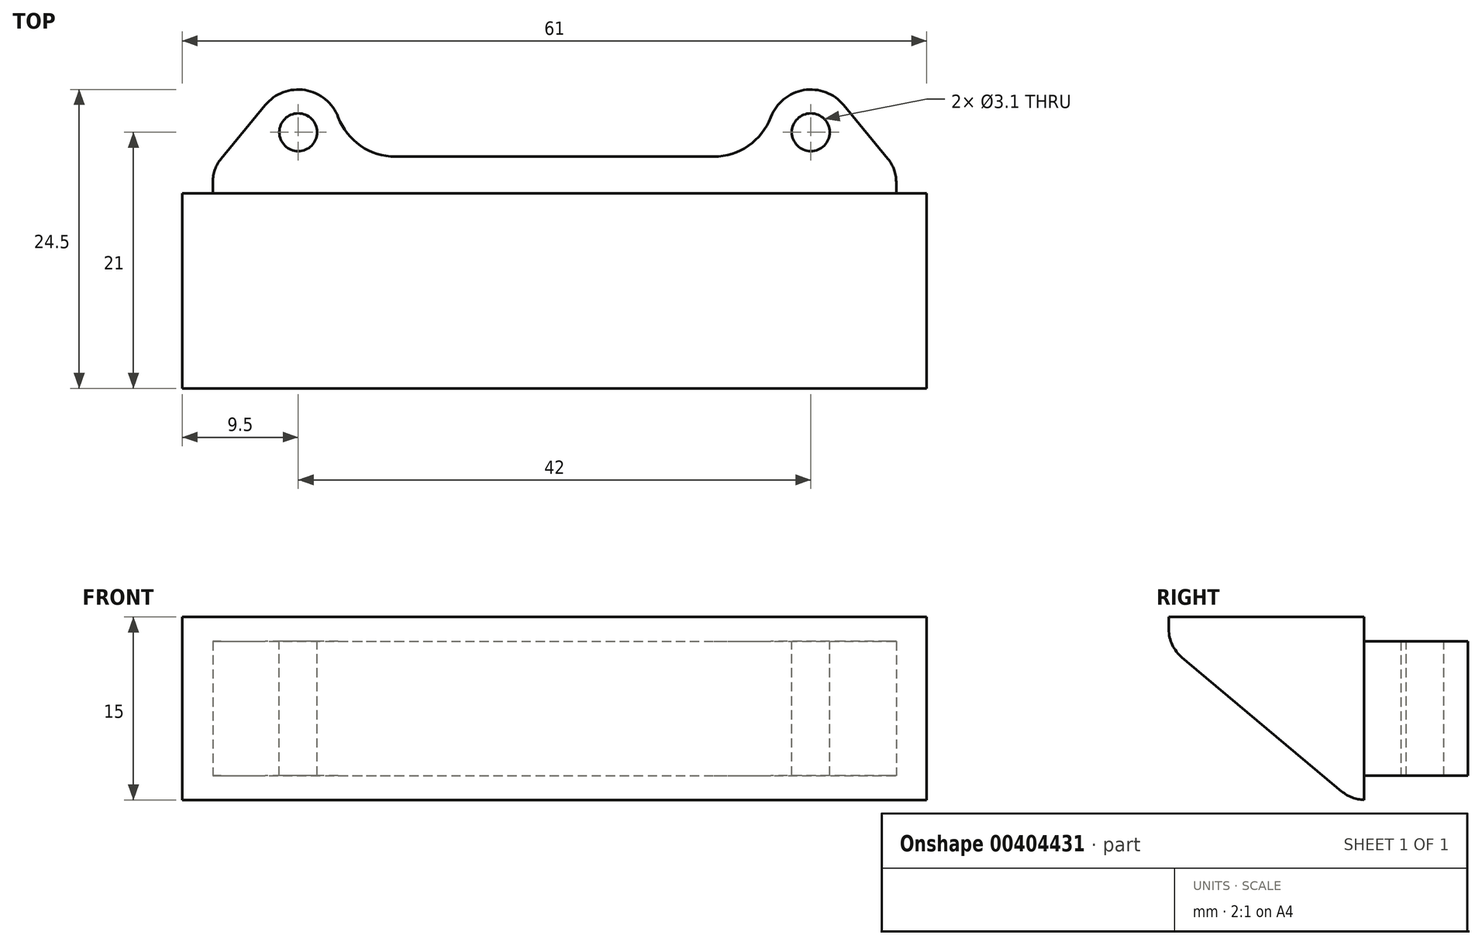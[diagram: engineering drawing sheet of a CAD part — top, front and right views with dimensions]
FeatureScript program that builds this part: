
annotation { "Feature Type Name" : "Feature", "Feature Type Description" : "" }
export const myFeature = defineFeature(function(context is Context, id is Id, definition is map)
    precondition{}
    {
        {
            var Q0;
            Q0=qCreatedBy(makeId("Top.planeOp"),FACE);
            var sketch = newSketch(context, id + "F0", { "sketchPlane" : qUnion([Q0])});
            skCircle(sketch, "E0", {"center": v(-21, 5) * mm, "radius": 3.5 * mm});
            skCircle(sketch, "E1", {"center": v(21, 5) * mm, "radius": 3.5 * mm});
            skLineSegment(sketch, "E2", {"start": v(-21, 5) * mm, "end": v(21, 5) * mm, "construction": true});
            skLineSegment(sketch, "E3", {"start": v(0, 5) * mm, "end": v(0, 0) * mm});
            skLineSegment(sketch, "E4", {"start": v(30.5, -16) * mm, "end": v(-30.5, -16) * mm});
            skLineSegment(sketch, "E5", {"start": v(-30.5, -16) * mm, "end": v(-30.5, 0) * mm});
            skLineSegment(sketch, "E6", {"start": v(-30.5, 0) * mm, "end": v(-28, 0) * mm});
            skLineSegment(sketch, "E7", {"start": v(30.5, -16) * mm, "end": v(30.5, 0) * mm});
            skLineSegment(sketch, "E8", {"start": v(30.5, 0) * mm, "end": v(28, 0) * mm});
            skLineSegment(sketch, "E9", {"start": v(-17.5, 5) * mm, "end": v(-17.5, 3) * mm});
            skLineSegment(sketch, "E10", {"start": v(-17.5, 3) * mm, "end": v(17.5, 3) * mm});
            skLineSegment(sketch, "E11", {"start": v(17.5, 3) * mm, "end": v(17.5, 5) * mm});
            skLineSegment(sketch, "E12", {"start": v(-28, 0) * mm, "end": v(-28, 2) * mm});
            skLineSegment(sketch, "E13", {"start": v(-28, 2) * mm, "end": v(-23.7, 7.22) * mm});
            skLineSegment(sketch, "E14", {"start": v(28, 0) * mm, "end": v(28, 2) * mm});
            skLineSegment(sketch, "E15", {"start": v(28, 2) * mm, "end": v(23.7, 7.22) * mm});
            skLineSegment(sketch, "E16", {"start": v(0, -16) * mm, "end": v(0, 0) * mm});
            skLineSegment(sketch, "E17", {"start": v(-28, 0) * mm, "end": v(28, 0) * mm});
            skSolve(sketch);
        }
        {
            var Q0;
            {var subQ1=sQuery(id+"F0.wireOp",EDGE,"E7");Q0=makeQuery(id+"F0.imprint","IMPRINT",FACE,{"disambiguationData":[TD([[makeQuery(id+"F0.imprint","IMPRINT",EDGE,{"derivedFrom":subQ1}),1.0]])]});}
            var Q1;
            {var subQ2=sQuery(id+"F0.wireOp",EDGE,"E5");Q1=makeQuery(id+"F0.imprint","IMPRINT",FACE,{"disambiguationData":[TD([[makeQuery(id+"F0.imprint","IMPRINT",EDGE,{"derivedFrom":subQ2}),-1.0]])]});}
            extrude(context, id + "F1", {"entities" : qUnion([Q0, Q1]), "endBound" : BoundingType.SYMMETRIC, "depth" : 15 * mm});
        }
        {
            var Q0;
            {var subQ1=sQuery(id+"F0.wireOp",EDGE,"E9");Q0=makeQuery(id+"F0.imprint","IMPRINT",FACE,{"disambiguationData":[TD([[makeQuery(id+"F0.imprint","IMPRINT",EDGE,{"derivedFrom":subQ1}),-1.0]])]});}
            var Q1;
            {var subQ0=sQuery(id+"F0.wireOp",EDGE,"E0");var subQ1=makeQuery(id+"F0.imprint","INTERSECT",VERTEX,{"derivedFrom":[subQ0,sQuery(id+"F0.wireOp",EDGE,"E9")]});Q1=makeQuery(id+"F0.imprint","IMPRINT",FACE,{"disambiguationData":[TD([[makeQuery(id+"F0.imprint","IMPRINT",EDGE,{"disambiguationData":[TD([[subQ1,1.0]])],"derivedFrom":subQ0}),1.0]])]});}
            var Q2;
            {var subQ0=sQuery(id+"F0.wireOp",EDGE,"E1");var subQ1=makeQuery(id+"F0.imprint","INTERSECT",VERTEX,{"derivedFrom":[subQ0,sQuery(id+"F0.wireOp",EDGE,"E11")]});Q2=makeQuery(id+"F0.imprint","IMPRINT",FACE,{"disambiguationData":[TD([[makeQuery(id+"F0.imprint","IMPRINT",EDGE,{"disambiguationData":[TD([[subQ1,1.0]])],"derivedFrom":subQ0}),1.0]])]});}
            var Q3;
            {var subQ0=sQuery(id+"F0.wireOp",EDGE,"E11");Q3=makeQuery(id+"F0.imprint","IMPRINT",FACE,{"disambiguationData":[TD([[makeQuery(id+"F0.imprint","IMPRINT",EDGE,{"derivedFrom":subQ0}),-1.0]])]});}
            extrude(context, id + "F2", {"entities" : qUnion([Q0, Q1, Q2, Q3]), "operationType" : NewBodyOperationType.ADD, "endBound" : BoundingType.SYMMETRIC, "depth" : 11 * mm});
        }
        {
            var Q0;
            Q0=makeQuery(id+"F1.opExtrude","CAP_EDGE",EDGE,{"disambiguationData":[OSD([sQuery(id+"F0.wireOp",EDGE,"E4")])],"isStart":true});
            chamfer(context, id + "F3", {"entities" : qUnion([Q0]), "chamferType" : ChamferType.OFFSET_ANGLE, "width" : 15 * mm, "oppositeDirection" : false, "angle" : 40 * degree, "tangentPropagation" : true});
        }
        {
            var Q0;
            Q0=makeQuery(id+"F2.opExtrude","CAP_FACE",FACE,{"disambiguationData":[OSD([sQuery(id+"F0.wireOp",EDGE,"E0"),sQuery(id+"F0.wireOp",EDGE,"E1"),sQuery(id+"F0.wireOp",EDGE,"E9"),sQuery(id+"F0.wireOp",EDGE,"E10"),sQuery(id+"F0.wireOp",EDGE,"E11"),sQuery(id+"F0.wireOp",EDGE,"E12"),sQuery(id+"F0.wireOp",EDGE,"E13"),sQuery(id+"F0.wireOp",EDGE,"E14"),sQuery(id+"F0.wireOp",EDGE,"E15"),sQuery(id+"F0.wireOp",EDGE,"E17")])],"isStart":false});
            var sketch = newSketch(context, id + "F4", { "sketchPlane" : qUnion([Q0])});
            skPoint(sketch, "E18", {"position": v(-21, 5) * mm});
            skPoint(sketch, "E19", {"position": v(21, 5) * mm});
            skSolve(sketch);
        }
        {
            var Q0;
            Q0=sQuery(id+"F4.wireOp",VERTEX,"E18");
            var Q1;
            Q1=sQuery(id+"F4.wireOp",VERTEX,"E19");
            var Q2;
            Q2=makeQuery(id+"F1.opExtrude","SWEPT_BODY",BODY,{"disambiguationData":[OSD([sQuery(id+"F0.wireOp",EDGE,"E4"),sQuery(id+"F0.wireOp",EDGE,"E5"),sQuery(id+"F0.wireOp",EDGE,"E6"),sQuery(id+"F0.wireOp",EDGE,"E7"),sQuery(id+"F0.wireOp",EDGE,"E8"),sQuery(id+"F0.wireOp",EDGE,"E17")])]});
            hole(context, id + "F5", {"style" : HoleStyle.SIMPLE, "endStyle" : HoleEndStyle.THROUGH, "holeDiameter" : 3.1 * mm, "tappedDepth" : 12 * mm, "tapClearance" : 3, "locations" : qUnion([Q0, Q1]), "scope" : qUnion([Q2])});
        }
        {
            var Q0;
            {var subQ0=sQuery(id+"F0.wireOp",EDGE,"E4");Q0=makeQuery(id+"F3.opChamfer","BLEND_EDGE",EDGE,{"blendedFrom":[makeQuery(id+"F1.opExtrude","CAP_EDGE",EDGE,{"disambiguationData":[OSD([subQ0])],"isStart":true}),makeQuery(id+"F1.opExtrude","SWEPT_FACE",FACE,{"disambiguationData":[OSD([subQ0])]})],"blendedInto":[makeQuery(id+"F1.opExtrude","SWEPT_FACE",FACE,{"disambiguationData":[OSD([subQ0])]})]});}
            fillet(context, id + "F6", {"entities" : qUnion([Q0]), "radius" : 3 * mm, "tangentPropagation" : true, "allowEdgeOverflow" : false});
        }
        {
            var Q0;
            {var subQ0=sQuery(id+"F0.wireOp",EDGE,"E4");Q0=makeQuery(id+"F3.opChamfer","BLEND_EDGE",EDGE,{"blendedFrom":[makeQuery(id+"F1.opExtrude","CAP_EDGE",EDGE,{"disambiguationData":[OSD([subQ0])],"isStart":true}),makeQuery(id+"F1.opExtrude","CAP_FACE",FACE,{"disambiguationData":[OSD([subQ0,sQuery(id+"F0.wireOp",EDGE,"E5"),sQuery(id+"F0.wireOp",EDGE,"E6"),sQuery(id+"F0.wireOp",EDGE,"E7"),sQuery(id+"F0.wireOp",EDGE,"E8"),sQuery(id+"F0.wireOp",EDGE,"E17")])],"isStart":true})],"blendedInto":[makeQuery(id+"F1.opExtrude","CAP_FACE",FACE,{"disambiguationData":[OSD([subQ0,sQuery(id+"F0.wireOp",EDGE,"E5"),sQuery(id+"F0.wireOp",EDGE,"E6"),sQuery(id+"F0.wireOp",EDGE,"E7"),sQuery(id+"F0.wireOp",EDGE,"E8"),sQuery(id+"F0.wireOp",EDGE,"E17")])],"isStart":true})]});}
            var Q1;
            Q1=makeQuery(id+"F2.opExtrude","SWEPT_EDGE",EDGE,{"disambiguationData":[OSD([sQuery(id+"F0.wireOp",EDGE,"E12"),sQuery(id+"F0.wireOp",EDGE,"E13")])]});
            var Q2;
            Q2=makeQuery(id+"F2.opExtrude","SWEPT_EDGE",EDGE,{"disambiguationData":[OSD([sQuery(id+"F0.wireOp",EDGE,"E14"),sQuery(id+"F0.wireOp",EDGE,"E15")])]});
            fillet(context, id + "F7", {"entities" : qUnion([Q0, Q1, Q2]), "radius" : 3 * mm, "tangentPropagation" : true, "allowEdgeOverflow" : false});
        }
        {
            var Q0;
            Q0=makeQuery(id+"F2.opExtrude","SWEPT_EDGE",EDGE,{"disambiguationData":[OSD([sQuery(id+"F0.wireOp",EDGE,"E10"),sQuery(id+"F0.wireOp",EDGE,"E11")])]});
            var Q1;
            Q1=makeQuery(id+"F2.opExtrude","SWEPT_EDGE",EDGE,{"disambiguationData":[OSD([sQuery(id+"F0.wireOp",EDGE,"E9"),sQuery(id+"F0.wireOp",EDGE,"E10")])]});
            fillet(context, id + "F8", {"entities" : qUnion([Q0, Q1]), "radius" : 5 * mm, "tangentPropagation" : true, "allowEdgeOverflow" : false});
        }
    });
